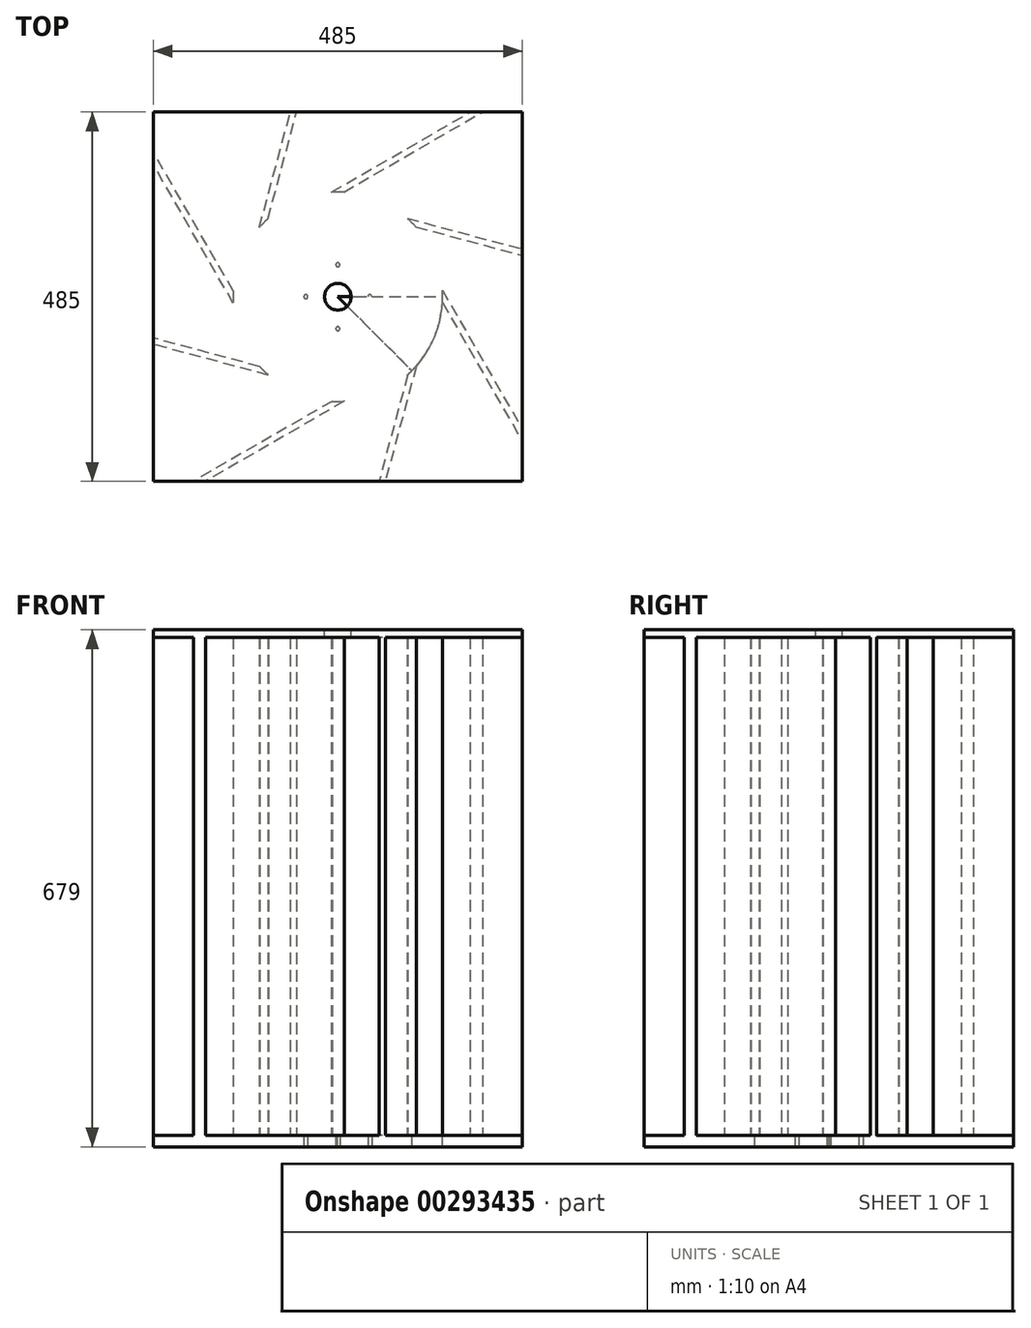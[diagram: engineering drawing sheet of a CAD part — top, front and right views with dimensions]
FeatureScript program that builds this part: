
annotation { "Feature Type Name" : "Feature", "Feature Type Description" : "" }
export const myFeature = defineFeature(function(context is Context, id is Id, definition is map)
    precondition{}
    {
        {
            var Q0;
            Q0=qCreatedBy(makeId("Top.planeOp"),FACE);
            var sketch = newSketch(context, id + "F0", { "sketchPlane" : qUnion([Q0])});
            skCircle(sketch, "E0", {"center": v(0, 0) * mm, "radius": 135 * mm});
            skLineSegment(sketch, "E1.bottom", {"start": v(242.5, -242.5) * mm, "end": v(-242.5, -242.5) * mm});
            skLineSegment(sketch, "E1.top", {"start": v(242.5, 242.5) * mm, "end": v(-242.5, 242.5) * mm});
            skLineSegment(sketch, "E1.left", {"start": v(242.5, -242.5) * mm, "end": v(242.5, 242.5) * mm});
            skLineSegment(sketch, "E1.right", {"start": v(-242.5, -242.5) * mm, "end": v(-242.5, 242.5) * mm});
            skCircle(sketch, "E2", {"center": v(0, 0) * mm, "radius": 137.5 * mm});
            skLineSegment(sketch, "E3", {"start": v(0, 242.5) * mm, "end": v(0, -242.5) * mm});
            skLineSegment(sketch, "E4", {"start": v(-242.5, 0) * mm, "end": v(242.5, 0) * mm});
            skLineSegment(sketch, "E5", {"start": v(-242.5, -242.5) * mm, "end": v(242.5, 242.5) * mm});
            skLineSegment(sketch, "E6", {"start": v(-242.5, 242.5) * mm, "end": v(242.5, -242.5) * mm});
            skLineSegment(sketch, "E7", {"start": v(0, 137.5) * mm, "end": v(181.87, 242.5) * mm});
            skLineSegment(sketch, "E8", {"start": v(-97.23, 97.23) * mm, "end": v(-58.3, 242.5) * mm});
            skLineSegment(sketch, "E9", {"start": v(-137.5, 0) * mm, "end": v(-242.5, 181.87) * mm});
            skLineSegment(sketch, "E10", {"start": v(-97.23, -97.23) * mm, "end": v(-242.5, -58.3) * mm});
            skLineSegment(sketch, "E11", {"start": v(0, -137.5) * mm, "end": v(-181.87, -242.5) * mm});
            skLineSegment(sketch, "E12", {"start": v(97.23, -97.23) * mm, "end": v(58.3, -242.5) * mm});
            skLineSegment(sketch, "E13", {"start": v(137.5, 0) * mm, "end": v(242.5, -181.87) * mm});
            skLineSegment(sketch, "E14", {"start": v(97.23, 97.23) * mm, "end": v(242.5, 58.3) * mm});
            skLineSegment(sketch, "E15.0", {"start": v(-91.68, 102.47) * mm, "end": v(-54.16, 242.5) * mm});
            skLineSegment(sketch, "E16.0", {"start": v(-103.02, 91.07) * mm, "end": v(-62.44, 242.5) * mm});
            skLineSegment(sketch, "E17.0", {"start": v(7.63, 137.29) * mm, "end": v(189.87, 242.5) * mm});
            skLineSegment(sketch, "E18.0", {"start": v(-8.45, 137.24) * mm, "end": v(173.87, 242.5) * mm});
            skLineSegment(sketch, "E19.0", {"start": v(102.47, 91.68) * mm, "end": v(242.5, 54.16) * mm});
            skLineSegment(sketch, "E20.0", {"start": v(91.07, 103.02) * mm, "end": v(242.5, 62.44) * mm});
            skLineSegment(sketch, "E21.0", {"start": v(137.29, -7.63) * mm, "end": v(242.5, -189.87) * mm});
            skLineSegment(sketch, "E22.0", {"start": v(137.24, 8.45) * mm, "end": v(242.5, -173.87) * mm});
            skLineSegment(sketch, "E23.0", {"start": v(-137.29, 7.63) * mm, "end": v(-242.5, 189.87) * mm});
            skLineSegment(sketch, "E24.0", {"start": v(-137.24, -8.45) * mm, "end": v(-242.5, 173.87) * mm});
            skLineSegment(sketch, "E25.0", {"start": v(-102.47, -91.68) * mm, "end": v(-242.5, -54.16) * mm});
            skLineSegment(sketch, "E26.0", {"start": v(-91.07, -103.02) * mm, "end": v(-242.5, -62.44) * mm});
            skLineSegment(sketch, "E27.0", {"start": v(-7.63, -137.29) * mm, "end": v(-189.87, -242.5) * mm});
            skLineSegment(sketch, "E28.0", {"start": v(8.45, -137.24) * mm, "end": v(-173.87, -242.5) * mm});
            skLineSegment(sketch, "E29.0", {"start": v(91.68, -102.47) * mm, "end": v(54.16, -242.5) * mm});
            skLineSegment(sketch, "E30.0", {"start": v(103.02, -91.07) * mm, "end": v(62.44, -242.5) * mm});
            skSolve(sketch);
        }
        {
            var Q0;
            {var subQ1=sQuery(id+"F0.wireOp",EDGE,"E1.top");var subQ3=sQuery(id+"F0.wireOp",EDGE,"E16.0");var subQ4=makeQuery(id+"F0.imprint","INTERSECT",VERTEX,{"derivedFrom":[subQ1,subQ3]});Q0=makeQuery(id+"F0.imprint","IMPRINT",FACE,{"disambiguationData":[TD([[makeQuery(id+"F0.imprint","IMPRINT",EDGE,{"disambiguationData":[TD([[subQ4,1.0]])],"derivedFrom":subQ3}),1.0]])]});}
            var Q1;
            {var subQ7=sQuery(id+"F0.wireOp",EDGE,"E23.0");Q1=makeQuery(id+"F0.imprint","IMPRINT",FACE,{"disambiguationData":[TD([[makeQuery(id+"F0.imprint","IMPRINT",EDGE,{"derivedFrom":subQ7}),-1.0]])]});}
            var Q2;
            {var subQ0=sQuery(id+"F0.wireOp",EDGE,"E5");var subQ5=sQuery(id+"F0.wireOp",EDGE,"E0");var subQ6=makeQuery(id+"F0.imprint","INTERSECT",VERTEX,{"disambiguationData":[OD(0.0)],"derivedFrom":[subQ5,subQ0]});Q2=makeQuery(id+"F0.imprint","IMPRINT",FACE,{"disambiguationData":[TD([[makeQuery(id+"F0.imprint","IMPRINT",EDGE,{"disambiguationData":[TD([[subQ6,1.0]])],"derivedFrom":subQ5}),-1.0]])]});}
            var Q3;
            {var subQ0=sQuery(id+"F0.wireOp",EDGE,"E5");var subQ1=sQuery(id+"F0.wireOp",EDGE,"E0");var subQ2=makeQuery(id+"F0.imprint","INTERSECT",VERTEX,{"disambiguationData":[OD(1.0)],"derivedFrom":[subQ1,subQ0]});Q3=makeQuery(id+"F0.imprint","IMPRINT",FACE,{"disambiguationData":[TD([[makeQuery(id+"F0.imprint","IMPRINT",EDGE,{"disambiguationData":[TD([[subQ2,-1.0]])],"derivedFrom":subQ1}),1.0]])]});}
            var Q4;
            {var subQ5=sQuery(id+"F0.wireOp",EDGE,"E29.0");Q4=makeQuery(id+"F0.imprint","IMPRINT",FACE,{"disambiguationData":[TD([[makeQuery(id+"F0.imprint","IMPRINT",EDGE,{"derivedFrom":subQ5}),-1.0]])]});}
            var Q5;
            {var subQ1=sQuery(id+"F0.wireOp",EDGE,"E1.bottom");var subQ3=sQuery(id+"F0.wireOp",EDGE,"E30.0");var subQ4=makeQuery(id+"F0.imprint","INTERSECT",VERTEX,{"derivedFrom":[subQ1,subQ3]});Q5=makeQuery(id+"F0.imprint","IMPRINT",FACE,{"disambiguationData":[TD([[makeQuery(id+"F0.imprint","IMPRINT",EDGE,{"disambiguationData":[TD([[subQ4,1.0]])],"derivedFrom":subQ3}),1.0]])]});}
            var Q6;
            {var subQ0=sQuery(id+"F0.wireOp",EDGE,"E3");var subQ1=sQuery(id+"F0.wireOp",EDGE,"E1.bottom");var subQ2=makeQuery(id+"F0.imprint","INTERSECT",VERTEX,{"derivedFrom":[subQ1,subQ0]});Q6=makeQuery(id+"F0.imprint","IMPRINT",FACE,{"disambiguationData":[TD([[makeQuery(id+"F0.imprint","IMPRINT",EDGE,{"disambiguationData":[TD([[subQ2,-1.0]])],"derivedFrom":subQ1}),-1.0]])]});}
            var Q7;
            {var subQ0=sQuery(id+"F0.wireOp",EDGE,"E3");var subQ1=sQuery(id+"F0.wireOp",EDGE,"E0");var subQ2=makeQuery(id+"F0.imprint","INTERSECT",VERTEX,{"disambiguationData":[OD(1.0)],"derivedFrom":[subQ1,subQ0]});Q7=makeQuery(id+"F0.imprint","IMPRINT",FACE,{"disambiguationData":[TD([[makeQuery(id+"F0.imprint","IMPRINT",EDGE,{"disambiguationData":[TD([[subQ2,-1.0]])],"derivedFrom":subQ1}),1.0]])]});}
            var Q8;
            {var subQ0=sQuery(id+"F0.wireOp",EDGE,"E4");var subQ1=sQuery(id+"F0.wireOp",EDGE,"E0");var subQ2=makeQuery(id+"F0.imprint","INTERSECT",VERTEX,{"disambiguationData":[OD(0.0)],"derivedFrom":[subQ1,subQ0]});Q8=makeQuery(id+"F0.imprint","IMPRINT",FACE,{"disambiguationData":[TD([[makeQuery(id+"F0.imprint","IMPRINT",EDGE,{"disambiguationData":[TD([[subQ2,1.0]])],"derivedFrom":subQ1}),1.0]])]});}
            var Q9;
            {var subQ4=sQuery(id+"F0.wireOp",EDGE,"E0");var subQ7=sQuery(id+"F0.wireOp",EDGE,"E3");var subQ9=makeQuery(id+"F0.imprint","INTERSECT",VERTEX,{"disambiguationData":[OD(1.0)],"derivedFrom":[subQ4,subQ7]});Q9=makeQuery(id+"F0.imprint","IMPRINT",FACE,{"disambiguationData":[TD([[makeQuery(id+"F0.imprint","IMPRINT",EDGE,{"disambiguationData":[TD([[subQ9,-1.0]])],"derivedFrom":subQ4}),-1.0]])]});}
            var Q10;
            {var subQ4=sQuery(id+"F0.wireOp",EDGE,"E3");var subQ7=sQuery(id+"F0.wireOp",EDGE,"E0");var subQ8=makeQuery(id+"F0.imprint","INTERSECT",VERTEX,{"disambiguationData":[OD(0.0)],"derivedFrom":[subQ7,subQ4]});Q10=makeQuery(id+"F0.imprint","IMPRINT",FACE,{"disambiguationData":[TD([[makeQuery(id+"F0.imprint","IMPRINT",EDGE,{"disambiguationData":[TD([[subQ8,-1.0]])],"derivedFrom":subQ7}),-1.0]])]});}
            var Q11;
            {var subQ0=sQuery(id+"F0.wireOp",EDGE,"E21.0");Q11=makeQuery(id+"F0.imprint","IMPRINT",FACE,{"disambiguationData":[TD([[makeQuery(id+"F0.imprint","IMPRINT",EDGE,{"derivedFrom":subQ0}),-1.0]])]});}
            var Q12;
            {var subQ0=sQuery(id+"F0.wireOp",EDGE,"E4");var subQ7=sQuery(id+"F0.wireOp",EDGE,"E0");var subQ8=makeQuery(id+"F0.imprint","INTERSECT",VERTEX,{"disambiguationData":[OD(0.0)],"derivedFrom":[subQ7,subQ0]});Q12=makeQuery(id+"F0.imprint","IMPRINT",FACE,{"disambiguationData":[TD([[makeQuery(id+"F0.imprint","IMPRINT",EDGE,{"disambiguationData":[TD([[subQ8,1.0]])],"derivedFrom":subQ7}),-1.0]])]});}
            var Q13;
            {var subQ0=sQuery(id+"F0.wireOp",EDGE,"E4");var subQ1=sQuery(id+"F0.wireOp",EDGE,"E0");var subQ2=makeQuery(id+"F0.imprint","INTERSECT",VERTEX,{"disambiguationData":[OD(1.0)],"derivedFrom":[subQ1,subQ0]});Q13=makeQuery(id+"F0.imprint","IMPRINT",FACE,{"disambiguationData":[TD([[makeQuery(id+"F0.imprint","IMPRINT",EDGE,{"disambiguationData":[TD([[subQ2,-1.0]])],"derivedFrom":subQ1}),1.0]])]});}
            var Q14;
            {var subQ0=sQuery(id+"F0.wireOp",EDGE,"E6");var subQ1=sQuery(id+"F0.wireOp",EDGE,"E0");var subQ2=makeQuery(id+"F0.imprint","INTERSECT",VERTEX,{"disambiguationData":[OD(0.0)],"derivedFrom":[subQ1,subQ0]});Q14=makeQuery(id+"F0.imprint","IMPRINT",FACE,{"disambiguationData":[TD([[makeQuery(id+"F0.imprint","IMPRINT",EDGE,{"disambiguationData":[TD([[subQ2,-1.0]])],"derivedFrom":subQ1}),1.0]])]});}
            var Q15;
            {var subQ4=sQuery(id+"F0.wireOp",EDGE,"E5");var subQ5=sQuery(id+"F0.wireOp",EDGE,"E0");var subQ6=makeQuery(id+"F0.imprint","INTERSECT",VERTEX,{"disambiguationData":[OD(0.0)],"derivedFrom":[subQ5,subQ4]});Q15=makeQuery(id+"F0.imprint","IMPRINT",FACE,{"disambiguationData":[TD([[makeQuery(id+"F0.imprint","IMPRINT",EDGE,{"disambiguationData":[TD([[subQ6,-1.0]])],"derivedFrom":subQ5}),-1.0]])]});}
            var Q16;
            {var subQ7=sQuery(id+"F0.wireOp",EDGE,"E25.0");Q16=makeQuery(id+"F0.imprint","IMPRINT",FACE,{"disambiguationData":[TD([[makeQuery(id+"F0.imprint","IMPRINT",EDGE,{"derivedFrom":subQ7}),-1.0]])]});}
            var Q17;
            {var subQ5=sQuery(id+"F0.wireOp",EDGE,"E5");var subQ7=sQuery(id+"F0.wireOp",EDGE,"E0");var subQ8=makeQuery(id+"F0.imprint","INTERSECT",VERTEX,{"disambiguationData":[OD(1.0)],"derivedFrom":[subQ7,subQ5]});Q17=makeQuery(id+"F0.imprint","IMPRINT",FACE,{"disambiguationData":[TD([[makeQuery(id+"F0.imprint","IMPRINT",EDGE,{"disambiguationData":[TD([[subQ8,-1.0]])],"derivedFrom":subQ7}),-1.0]])]});}
            var Q18;
            {var subQ0=sQuery(id+"F0.wireOp",EDGE,"E3");var subQ1=sQuery(id+"F0.wireOp",EDGE,"E0");var subQ2=makeQuery(id+"F0.imprint","INTERSECT",VERTEX,{"disambiguationData":[OD(0.0)],"derivedFrom":[subQ1,subQ0]});Q18=makeQuery(id+"F0.imprint","IMPRINT",FACE,{"disambiguationData":[TD([[makeQuery(id+"F0.imprint","IMPRINT",EDGE,{"disambiguationData":[TD([[subQ2,-1.0]])],"derivedFrom":subQ1}),1.0]])]});}
            var Q19;
            {var subQ0=sQuery(id+"F0.wireOp",EDGE,"E5");var subQ1=sQuery(id+"F0.wireOp",EDGE,"E0");var subQ2=makeQuery(id+"F0.imprint","INTERSECT",VERTEX,{"disambiguationData":[OD(0.0)],"derivedFrom":[subQ1,subQ0]});Q19=makeQuery(id+"F0.imprint","IMPRINT",FACE,{"disambiguationData":[TD([[makeQuery(id+"F0.imprint","IMPRINT",EDGE,{"disambiguationData":[TD([[subQ2,1.0]])],"derivedFrom":subQ1}),1.0]])]});}
            var Q20;
            {var subQ0=sQuery(id+"F0.wireOp",EDGE,"E5");var subQ1=sQuery(id+"F0.wireOp",EDGE,"E0");var subQ2=makeQuery(id+"F0.imprint","INTERSECT",VERTEX,{"disambiguationData":[OD(0.0)],"derivedFrom":[subQ1,subQ0]});Q20=makeQuery(id+"F0.imprint","IMPRINT",FACE,{"disambiguationData":[TD([[makeQuery(id+"F0.imprint","IMPRINT",EDGE,{"disambiguationData":[TD([[subQ2,-1.0]])],"derivedFrom":subQ1}),1.0]])]});}
            var Q21;
            {var subQ0=sQuery(id+"F0.wireOp",EDGE,"E4");var subQ1=sQuery(id+"F0.wireOp",EDGE,"E1.right");var subQ2=makeQuery(id+"F0.imprint","INTERSECT",VERTEX,{"derivedFrom":[subQ1,subQ0]});Q21=makeQuery(id+"F0.imprint","IMPRINT",FACE,{"disambiguationData":[TD([[makeQuery(id+"F0.imprint","IMPRINT",EDGE,{"disambiguationData":[TD([[subQ2,-1.0]])],"derivedFrom":subQ1}),-1.0]])]});}
            var Q22;
            {var subQ1=sQuery(id+"F0.wireOp",EDGE,"E1.right");var subQ3=sQuery(id+"F0.wireOp",EDGE,"E26.0");var subQ4=makeQuery(id+"F0.imprint","INTERSECT",VERTEX,{"derivedFrom":[subQ1,subQ3]});Q22=makeQuery(id+"F0.imprint","IMPRINT",FACE,{"disambiguationData":[TD([[makeQuery(id+"F0.imprint","IMPRINT",EDGE,{"disambiguationData":[TD([[subQ4,1.0]])],"derivedFrom":subQ3}),1.0]])]});}
            var Q23;
            {var subQ0=sQuery(id+"F0.wireOp",EDGE,"E4");var subQ1=sQuery(id+"F0.wireOp",EDGE,"E1.left");var subQ2=makeQuery(id+"F0.imprint","INTERSECT",VERTEX,{"derivedFrom":[subQ1,subQ0]});Q23=makeQuery(id+"F0.imprint","IMPRINT",FACE,{"disambiguationData":[TD([[makeQuery(id+"F0.imprint","IMPRINT",EDGE,{"disambiguationData":[TD([[subQ2,1.0]])],"derivedFrom":subQ1}),1.0]])]});}
            var Q24;
            {var subQ3=sQuery(id+"F0.wireOp",EDGE,"E4");var subQ5=sQuery(id+"F0.wireOp",EDGE,"E0");var subQ6=makeQuery(id+"F0.imprint","INTERSECT",VERTEX,{"disambiguationData":[OD(1.0)],"derivedFrom":[subQ5,subQ3]});Q24=makeQuery(id+"F0.imprint","IMPRINT",FACE,{"disambiguationData":[TD([[makeQuery(id+"F0.imprint","IMPRINT",EDGE,{"disambiguationData":[TD([[subQ6,-1.0]])],"derivedFrom":subQ5}),-1.0]])]});}
            var Q25;
            {var subQ0=sQuery(id+"F0.wireOp",EDGE,"E19.0");Q25=makeQuery(id+"F0.imprint","IMPRINT",FACE,{"disambiguationData":[TD([[makeQuery(id+"F0.imprint","IMPRINT",EDGE,{"derivedFrom":subQ0}),-1.0]])]});}
            var Q26;
            {var subQ3=sQuery(id+"F0.wireOp",EDGE,"E27.0");Q26=makeQuery(id+"F0.imprint","IMPRINT",FACE,{"disambiguationData":[TD([[makeQuery(id+"F0.imprint","IMPRINT",EDGE,{"derivedFrom":subQ3}),-1.0]])]});}
            var Q27;
            {var subQ5=sQuery(id+"F0.wireOp",EDGE,"E6");var subQ7=sQuery(id+"F0.wireOp",EDGE,"E0");var subQ8=makeQuery(id+"F0.imprint","INTERSECT",VERTEX,{"disambiguationData":[OD(0.0)],"derivedFrom":[subQ7,subQ5]});Q27=makeQuery(id+"F0.imprint","IMPRINT",FACE,{"disambiguationData":[TD([[makeQuery(id+"F0.imprint","IMPRINT",EDGE,{"disambiguationData":[TD([[subQ8,-1.0]])],"derivedFrom":subQ7}),-1.0]])]});}
            var Q28;
            {var subQ1=sQuery(id+"F0.wireOp",EDGE,"E2");var subQ3=sQuery(id+"F0.wireOp",EDGE,"E26.0");var subQ4=makeQuery(id+"F0.imprint","INTERSECT",VERTEX,{"derivedFrom":[subQ1,subQ3]});Q28=makeQuery(id+"F0.imprint","IMPRINT",FACE,{"disambiguationData":[TD([[makeQuery(id+"F0.imprint","IMPRINT",EDGE,{"disambiguationData":[TD([[subQ4,-1.0]])],"derivedFrom":subQ3}),-1.0]])]});}
            var Q29;
            {var subQ1=sQuery(id+"F0.wireOp",EDGE,"E2");var subQ3=sQuery(id+"F0.wireOp",EDGE,"E22.0");var subQ4=makeQuery(id+"F0.imprint","INTERSECT",VERTEX,{"derivedFrom":[subQ1,subQ3]});Q29=makeQuery(id+"F0.imprint","IMPRINT",FACE,{"disambiguationData":[TD([[makeQuery(id+"F0.imprint","IMPRINT",EDGE,{"disambiguationData":[TD([[subQ4,-1.0]])],"derivedFrom":subQ3}),-1.0]])]});}
            var Q30;
            {var subQ0=sQuery(id+"F0.wireOp",EDGE,"E11");Q30=makeQuery(id+"F0.imprint","IMPRINT",FACE,{"disambiguationData":[TD([[makeQuery(id+"F0.imprint","IMPRINT",EDGE,{"derivedFrom":subQ0}),1.0]])]});}
            var Q31;
            {var subQ0=sQuery(id+"F0.wireOp",EDGE,"E13");Q31=makeQuery(id+"F0.imprint","IMPRINT",FACE,{"disambiguationData":[TD([[makeQuery(id+"F0.imprint","IMPRINT",EDGE,{"derivedFrom":subQ0}),-1.0]])]});}
            var Q32;
            {var subQ0=sQuery(id+"F0.wireOp",EDGE,"E12");Q32=makeQuery(id+"F0.imprint","IMPRINT",FACE,{"disambiguationData":[TD([[makeQuery(id+"F0.imprint","IMPRINT",EDGE,{"derivedFrom":subQ0}),1.0]])]});}
            var Q33;
            {var subQ0=sQuery(id+"F0.wireOp",EDGE,"E8");Q33=makeQuery(id+"F0.imprint","IMPRINT",FACE,{"disambiguationData":[TD([[makeQuery(id+"F0.imprint","IMPRINT",EDGE,{"derivedFrom":subQ0}),-1.0]])]});}
            var Q34;
            {var subQ1=sQuery(id+"F0.wireOp",EDGE,"E2");var subQ3=sQuery(id+"F0.wireOp",EDGE,"E28.0");var subQ4=makeQuery(id+"F0.imprint","INTERSECT",VERTEX,{"derivedFrom":[subQ1,subQ3]});Q34=makeQuery(id+"F0.imprint","IMPRINT",FACE,{"disambiguationData":[TD([[makeQuery(id+"F0.imprint","IMPRINT",EDGE,{"disambiguationData":[TD([[subQ4,-1.0]])],"derivedFrom":subQ3}),-1.0]])]});}
            var Q35;
            {var subQ1=sQuery(id+"F0.wireOp",EDGE,"E2");var subQ3=sQuery(id+"F0.wireOp",EDGE,"E18.0");var subQ4=makeQuery(id+"F0.imprint","INTERSECT",VERTEX,{"derivedFrom":[subQ1,subQ3]});Q35=makeQuery(id+"F0.imprint","IMPRINT",FACE,{"disambiguationData":[TD([[makeQuery(id+"F0.imprint","IMPRINT",EDGE,{"disambiguationData":[TD([[subQ4,-1.0]])],"derivedFrom":subQ3}),-1.0]])]});}
            var Q36;
            {var subQ0=sQuery(id+"F0.wireOp",EDGE,"E10");Q36=makeQuery(id+"F0.imprint","IMPRINT",FACE,{"disambiguationData":[TD([[makeQuery(id+"F0.imprint","IMPRINT",EDGE,{"derivedFrom":subQ0}),1.0]])]});}
            var Q37;
            {var subQ0=sQuery(id+"F0.wireOp",EDGE,"E12");Q37=makeQuery(id+"F0.imprint","IMPRINT",FACE,{"disambiguationData":[TD([[makeQuery(id+"F0.imprint","IMPRINT",EDGE,{"derivedFrom":subQ0}),-1.0]])]});}
            var Q38;
            {var subQ0=sQuery(id+"F0.wireOp",EDGE,"E9");Q38=makeQuery(id+"F0.imprint","IMPRINT",FACE,{"disambiguationData":[TD([[makeQuery(id+"F0.imprint","IMPRINT",EDGE,{"derivedFrom":subQ0}),1.0]])]});}
            var Q39;
            {var subQ0=sQuery(id+"F0.wireOp",EDGE,"E8");Q39=makeQuery(id+"F0.imprint","IMPRINT",FACE,{"disambiguationData":[TD([[makeQuery(id+"F0.imprint","IMPRINT",EDGE,{"derivedFrom":subQ0}),1.0]])]});}
            var Q40;
            {var subQ0=sQuery(id+"F0.wireOp",EDGE,"E14");Q40=makeQuery(id+"F0.imprint","IMPRINT",FACE,{"disambiguationData":[TD([[makeQuery(id+"F0.imprint","IMPRINT",EDGE,{"derivedFrom":subQ0}),1.0]])]});}
            var Q41;
            {var subQ0=sQuery(id+"F0.wireOp",EDGE,"E10");Q41=makeQuery(id+"F0.imprint","IMPRINT",FACE,{"disambiguationData":[TD([[makeQuery(id+"F0.imprint","IMPRINT",EDGE,{"derivedFrom":subQ0}),-1.0]])]});}
            var Q42;
            {var subQ0=sQuery(id+"F0.wireOp",EDGE,"E14");Q42=makeQuery(id+"F0.imprint","IMPRINT",FACE,{"disambiguationData":[TD([[makeQuery(id+"F0.imprint","IMPRINT",EDGE,{"derivedFrom":subQ0}),-1.0]])]});}
            var Q43;
            {var subQ0=sQuery(id+"F0.wireOp",EDGE,"E9");Q43=makeQuery(id+"F0.imprint","IMPRINT",FACE,{"disambiguationData":[TD([[makeQuery(id+"F0.imprint","IMPRINT",EDGE,{"derivedFrom":subQ0}),-1.0]])]});}
            var Q44;
            {var subQ1=sQuery(id+"F0.wireOp",EDGE,"E2");var subQ3=sQuery(id+"F0.wireOp",EDGE,"E16.0");var subQ4=makeQuery(id+"F0.imprint","INTERSECT",VERTEX,{"derivedFrom":[subQ1,subQ3]});Q44=makeQuery(id+"F0.imprint","IMPRINT",FACE,{"disambiguationData":[TD([[makeQuery(id+"F0.imprint","IMPRINT",EDGE,{"disambiguationData":[TD([[subQ4,-1.0]])],"derivedFrom":subQ3}),-1.0]])]});}
            var Q45;
            {var subQ0=sQuery(id+"F0.wireOp",EDGE,"E13");Q45=makeQuery(id+"F0.imprint","IMPRINT",FACE,{"disambiguationData":[TD([[makeQuery(id+"F0.imprint","IMPRINT",EDGE,{"derivedFrom":subQ0}),1.0]])]});}
            var Q46;
            {var subQ0=sQuery(id+"F0.wireOp",EDGE,"E11");Q46=makeQuery(id+"F0.imprint","IMPRINT",FACE,{"disambiguationData":[TD([[makeQuery(id+"F0.imprint","IMPRINT",EDGE,{"derivedFrom":subQ0}),-1.0]])]});}
            var Q47;
            {var subQ1=sQuery(id+"F0.wireOp",EDGE,"E2");var subQ3=sQuery(id+"F0.wireOp",EDGE,"E20.0");var subQ4=makeQuery(id+"F0.imprint","INTERSECT",VERTEX,{"derivedFrom":[subQ1,subQ3]});Q47=makeQuery(id+"F0.imprint","IMPRINT",FACE,{"disambiguationData":[TD([[makeQuery(id+"F0.imprint","IMPRINT",EDGE,{"disambiguationData":[TD([[subQ4,-1.0]])],"derivedFrom":subQ3}),-1.0]])]});}
            var Q48;
            {var subQ1=sQuery(id+"F0.wireOp",EDGE,"E2");var subQ3=sQuery(id+"F0.wireOp",EDGE,"E30.0");var subQ4=makeQuery(id+"F0.imprint","INTERSECT",VERTEX,{"derivedFrom":[subQ1,subQ3]});Q48=makeQuery(id+"F0.imprint","IMPRINT",FACE,{"disambiguationData":[TD([[makeQuery(id+"F0.imprint","IMPRINT",EDGE,{"disambiguationData":[TD([[subQ4,-1.0]])],"derivedFrom":subQ3}),-1.0]])]});}
            var Q49;
            {var subQ1=sQuery(id+"F0.wireOp",EDGE,"E2");var subQ3=sQuery(id+"F0.wireOp",EDGE,"E24.0");var subQ4=makeQuery(id+"F0.imprint","INTERSECT",VERTEX,{"derivedFrom":[subQ1,subQ3]});Q49=makeQuery(id+"F0.imprint","IMPRINT",FACE,{"disambiguationData":[TD([[makeQuery(id+"F0.imprint","IMPRINT",EDGE,{"disambiguationData":[TD([[subQ4,-1.0]])],"derivedFrom":subQ3}),-1.0]])]});}
            var Q50;
            {var subQ0=sQuery(id+"F0.wireOp",EDGE,"E15.0");Q50=makeQuery(id+"F0.imprint","IMPRINT",FACE,{"disambiguationData":[TD([[makeQuery(id+"F0.imprint","IMPRINT",EDGE,{"derivedFrom":subQ0}),-1.0]])]});}
            var Q51;
            {var subQ1=sQuery(id+"F0.wireOp",EDGE,"E1.left");var subQ3=sQuery(id+"F0.wireOp",EDGE,"E20.0");var subQ4=makeQuery(id+"F0.imprint","INTERSECT",VERTEX,{"derivedFrom":[subQ1,subQ3]});Q51=makeQuery(id+"F0.imprint","IMPRINT",FACE,{"disambiguationData":[TD([[makeQuery(id+"F0.imprint","IMPRINT",EDGE,{"disambiguationData":[TD([[subQ4,1.0]])],"derivedFrom":subQ3}),1.0]])]});}
            var Q52;
            {var subQ0=sQuery(id+"F0.wireOp",EDGE,"E3");var subQ1=sQuery(id+"F0.wireOp",EDGE,"E1.top");var subQ2=makeQuery(id+"F0.imprint","INTERSECT",VERTEX,{"derivedFrom":[subQ1,subQ0]});Q52=makeQuery(id+"F0.imprint","IMPRINT",FACE,{"disambiguationData":[TD([[makeQuery(id+"F0.imprint","IMPRINT",EDGE,{"disambiguationData":[TD([[subQ2,1.0]])],"derivedFrom":subQ1}),1.0]])]});}
            var Q53;
            {var subQ0=sQuery(id+"F0.wireOp",EDGE,"E17.0");Q53=makeQuery(id+"F0.imprint","IMPRINT",FACE,{"disambiguationData":[TD([[makeQuery(id+"F0.imprint","IMPRINT",EDGE,{"derivedFrom":subQ0}),-1.0]])]});}
            var Q54;
            {var subQ0=sQuery(id+"F0.wireOp",EDGE,"E7");Q54=makeQuery(id+"F0.imprint","IMPRINT",FACE,{"disambiguationData":[TD([[makeQuery(id+"F0.imprint","IMPRINT",EDGE,{"derivedFrom":subQ0}),1.0]])]});}
            var Q55;
            {var subQ0=sQuery(id+"F0.wireOp",EDGE,"E7");Q55=makeQuery(id+"F0.imprint","IMPRINT",FACE,{"disambiguationData":[TD([[makeQuery(id+"F0.imprint","IMPRINT",EDGE,{"derivedFrom":subQ0}),-1.0]])]});}
            extrude(context, id + "F1", {"entities" : qUnion([Q0, Q1, Q2, Q3, Q4, Q5, Q6, Q7, Q8, Q9, Q10, Q11, Q12, Q13, Q14, Q15, Q16, Q17, Q18, Q19, Q20, Q21, Q22, Q23, Q24, Q25, Q26, Q27, Q28, Q29, Q30, Q31, Q32, Q33, Q34, Q35, Q36, Q37, Q38, Q39, Q40, Q41, Q42, Q43, Q44, Q45, Q46, Q47, Q48, Q49, Q50, Q51, Q52, Q53, Q54, Q55]), "oppositeDirection" : true, "depth" : 15 * mm});
        }
        {
            var Q0;
            {var subQ0=sQuery(id+"F0.wireOp",EDGE,"E8");Q0=makeQuery(id+"F0.imprint","IMPRINT",FACE,{"disambiguationData":[TD([[makeQuery(id+"F0.imprint","IMPRINT",EDGE,{"derivedFrom":subQ0}),1.0]])]});}
            var Q1;
            {var subQ0=sQuery(id+"F0.wireOp",EDGE,"E8");Q1=makeQuery(id+"F0.imprint","IMPRINT",FACE,{"disambiguationData":[TD([[makeQuery(id+"F0.imprint","IMPRINT",EDGE,{"derivedFrom":subQ0}),-1.0]])]});}
            var Q2;
            {var subQ1=sQuery(id+"F0.wireOp",EDGE,"E2");var subQ3=sQuery(id+"F0.wireOp",EDGE,"E16.0");var subQ4=makeQuery(id+"F0.imprint","INTERSECT",VERTEX,{"derivedFrom":[subQ1,subQ3]});Q2=makeQuery(id+"F0.imprint","IMPRINT",FACE,{"disambiguationData":[TD([[makeQuery(id+"F0.imprint","IMPRINT",EDGE,{"disambiguationData":[TD([[subQ4,-1.0]])],"derivedFrom":subQ3}),-1.0]])]});}
            var Q3;
            {var subQ0=sQuery(id+"F0.wireOp",EDGE,"E7");Q3=makeQuery(id+"F0.imprint","IMPRINT",FACE,{"disambiguationData":[TD([[makeQuery(id+"F0.imprint","IMPRINT",EDGE,{"derivedFrom":subQ0}),1.0]])]});}
            var Q4;
            {var subQ0=sQuery(id+"F0.wireOp",EDGE,"E7");Q4=makeQuery(id+"F0.imprint","IMPRINT",FACE,{"disambiguationData":[TD([[makeQuery(id+"F0.imprint","IMPRINT",EDGE,{"derivedFrom":subQ0}),-1.0]])]});}
            var Q5;
            {var subQ1=sQuery(id+"F0.wireOp",EDGE,"E2");var subQ3=sQuery(id+"F0.wireOp",EDGE,"E18.0");var subQ4=makeQuery(id+"F0.imprint","INTERSECT",VERTEX,{"derivedFrom":[subQ1,subQ3]});Q5=makeQuery(id+"F0.imprint","IMPRINT",FACE,{"disambiguationData":[TD([[makeQuery(id+"F0.imprint","IMPRINT",EDGE,{"disambiguationData":[TD([[subQ4,-1.0]])],"derivedFrom":subQ3}),-1.0]])]});}
            var Q6;
            {var subQ0=sQuery(id+"F0.wireOp",EDGE,"E14");Q6=makeQuery(id+"F0.imprint","IMPRINT",FACE,{"disambiguationData":[TD([[makeQuery(id+"F0.imprint","IMPRINT",EDGE,{"derivedFrom":subQ0}),-1.0]])]});}
            var Q7;
            {var subQ0=sQuery(id+"F0.wireOp",EDGE,"E14");Q7=makeQuery(id+"F0.imprint","IMPRINT",FACE,{"disambiguationData":[TD([[makeQuery(id+"F0.imprint","IMPRINT",EDGE,{"derivedFrom":subQ0}),1.0]])]});}
            var Q8;
            {var subQ1=sQuery(id+"F0.wireOp",EDGE,"E2");var subQ3=sQuery(id+"F0.wireOp",EDGE,"E20.0");var subQ4=makeQuery(id+"F0.imprint","INTERSECT",VERTEX,{"derivedFrom":[subQ1,subQ3]});Q8=makeQuery(id+"F0.imprint","IMPRINT",FACE,{"disambiguationData":[TD([[makeQuery(id+"F0.imprint","IMPRINT",EDGE,{"disambiguationData":[TD([[subQ4,-1.0]])],"derivedFrom":subQ3}),-1.0]])]});}
            var Q9;
            {var subQ1=sQuery(id+"F0.wireOp",EDGE,"E2");var subQ3=sQuery(id+"F0.wireOp",EDGE,"E22.0");var subQ4=makeQuery(id+"F0.imprint","INTERSECT",VERTEX,{"derivedFrom":[subQ1,subQ3]});Q9=makeQuery(id+"F0.imprint","IMPRINT",FACE,{"disambiguationData":[TD([[makeQuery(id+"F0.imprint","IMPRINT",EDGE,{"disambiguationData":[TD([[subQ4,-1.0]])],"derivedFrom":subQ3}),-1.0]])]});}
            var Q10;
            {var subQ0=sQuery(id+"F0.wireOp",EDGE,"E13");Q10=makeQuery(id+"F0.imprint","IMPRINT",FACE,{"disambiguationData":[TD([[makeQuery(id+"F0.imprint","IMPRINT",EDGE,{"derivedFrom":subQ0}),1.0]])]});}
            var Q11;
            {var subQ0=sQuery(id+"F0.wireOp",EDGE,"E13");Q11=makeQuery(id+"F0.imprint","IMPRINT",FACE,{"disambiguationData":[TD([[makeQuery(id+"F0.imprint","IMPRINT",EDGE,{"derivedFrom":subQ0}),-1.0]])]});}
            var Q12;
            {var subQ0=sQuery(id+"F0.wireOp",EDGE,"E12");Q12=makeQuery(id+"F0.imprint","IMPRINT",FACE,{"disambiguationData":[TD([[makeQuery(id+"F0.imprint","IMPRINT",EDGE,{"derivedFrom":subQ0}),-1.0]])]});}
            var Q13;
            {var subQ0=sQuery(id+"F0.wireOp",EDGE,"E12");Q13=makeQuery(id+"F0.imprint","IMPRINT",FACE,{"disambiguationData":[TD([[makeQuery(id+"F0.imprint","IMPRINT",EDGE,{"derivedFrom":subQ0}),1.0]])]});}
            var Q14;
            {var subQ1=sQuery(id+"F0.wireOp",EDGE,"E2");var subQ3=sQuery(id+"F0.wireOp",EDGE,"E30.0");var subQ4=makeQuery(id+"F0.imprint","INTERSECT",VERTEX,{"derivedFrom":[subQ1,subQ3]});Q14=makeQuery(id+"F0.imprint","IMPRINT",FACE,{"disambiguationData":[TD([[makeQuery(id+"F0.imprint","IMPRINT",EDGE,{"disambiguationData":[TD([[subQ4,-1.0]])],"derivedFrom":subQ3}),-1.0]])]});}
            var Q15;
            {var subQ0=sQuery(id+"F0.wireOp",EDGE,"E11");Q15=makeQuery(id+"F0.imprint","IMPRINT",FACE,{"disambiguationData":[TD([[makeQuery(id+"F0.imprint","IMPRINT",EDGE,{"derivedFrom":subQ0}),-1.0]])]});}
            var Q16;
            {var subQ0=sQuery(id+"F0.wireOp",EDGE,"E11");Q16=makeQuery(id+"F0.imprint","IMPRINT",FACE,{"disambiguationData":[TD([[makeQuery(id+"F0.imprint","IMPRINT",EDGE,{"derivedFrom":subQ0}),1.0]])]});}
            var Q17;
            {var subQ1=sQuery(id+"F0.wireOp",EDGE,"E2");var subQ3=sQuery(id+"F0.wireOp",EDGE,"E28.0");var subQ4=makeQuery(id+"F0.imprint","INTERSECT",VERTEX,{"derivedFrom":[subQ1,subQ3]});Q17=makeQuery(id+"F0.imprint","IMPRINT",FACE,{"disambiguationData":[TD([[makeQuery(id+"F0.imprint","IMPRINT",EDGE,{"disambiguationData":[TD([[subQ4,-1.0]])],"derivedFrom":subQ3}),-1.0]])]});}
            var Q18;
            {var subQ1=sQuery(id+"F0.wireOp",EDGE,"E2");var subQ3=sQuery(id+"F0.wireOp",EDGE,"E26.0");var subQ4=makeQuery(id+"F0.imprint","INTERSECT",VERTEX,{"derivedFrom":[subQ1,subQ3]});Q18=makeQuery(id+"F0.imprint","IMPRINT",FACE,{"disambiguationData":[TD([[makeQuery(id+"F0.imprint","IMPRINT",EDGE,{"disambiguationData":[TD([[subQ4,-1.0]])],"derivedFrom":subQ3}),-1.0]])]});}
            var Q19;
            {var subQ0=sQuery(id+"F0.wireOp",EDGE,"E10");Q19=makeQuery(id+"F0.imprint","IMPRINT",FACE,{"disambiguationData":[TD([[makeQuery(id+"F0.imprint","IMPRINT",EDGE,{"derivedFrom":subQ0}),1.0]])]});}
            var Q20;
            {var subQ0=sQuery(id+"F0.wireOp",EDGE,"E10");Q20=makeQuery(id+"F0.imprint","IMPRINT",FACE,{"disambiguationData":[TD([[makeQuery(id+"F0.imprint","IMPRINT",EDGE,{"derivedFrom":subQ0}),-1.0]])]});}
            var Q21;
            {var subQ0=sQuery(id+"F0.wireOp",EDGE,"E9");Q21=makeQuery(id+"F0.imprint","IMPRINT",FACE,{"disambiguationData":[TD([[makeQuery(id+"F0.imprint","IMPRINT",EDGE,{"derivedFrom":subQ0}),-1.0]])]});}
            var Q22;
            {var subQ0=sQuery(id+"F0.wireOp",EDGE,"E9");Q22=makeQuery(id+"F0.imprint","IMPRINT",FACE,{"disambiguationData":[TD([[makeQuery(id+"F0.imprint","IMPRINT",EDGE,{"derivedFrom":subQ0}),1.0]])]});}
            var Q23;
            {var subQ1=sQuery(id+"F0.wireOp",EDGE,"E2");var subQ3=sQuery(id+"F0.wireOp",EDGE,"E24.0");var subQ4=makeQuery(id+"F0.imprint","INTERSECT",VERTEX,{"derivedFrom":[subQ1,subQ3]});Q23=makeQuery(id+"F0.imprint","IMPRINT",FACE,{"disambiguationData":[TD([[makeQuery(id+"F0.imprint","IMPRINT",EDGE,{"disambiguationData":[TD([[subQ4,-1.0]])],"derivedFrom":subQ3}),-1.0]])]});}
            extrude(context, id + "F2", {"entities" : qUnion([Q0, Q1, Q2, Q3, Q4, Q5, Q6, Q7, Q8, Q9, Q10, Q11, Q12, Q13, Q14, Q15, Q16, Q17, Q18, Q19, Q20, Q21, Q22, Q23]), "operationType" : NewBodyOperationType.ADD, "depth" : 654 * mm, "offsetDistance" : 25 * mm});
        }
        {
            var Q0;
            Q0=makeQuery(id+"F2.opExtrude","CAP_FACE",FACE,{"disambiguationData":[OSD([sQuery(id+"F0.wireOp",EDGE,"E1.left"),sQuery(id+"F0.wireOp",EDGE,"E2"),sQuery(id+"F0.wireOp",EDGE,"E19.0"),sQuery(id+"F0.wireOp",EDGE,"E20.0")])],"isStart":false});
            var sketch = newSketch(context, id + "F3", { "sketchPlane" : qUnion([Q0])});
            skLineSegment(sketch, "E31.bottom", {"start": v(242.5, -242.5) * mm, "end": v(-242.5, -242.5) * mm});
            skLineSegment(sketch, "E31.top", {"start": v(242.5, 242.5) * mm, "end": v(-242.5, 242.5) * mm});
            skLineSegment(sketch, "E31.left", {"start": v(242.5, -242.5) * mm, "end": v(242.5, 242.5) * mm});
            skLineSegment(sketch, "E31.right", {"start": v(-242.5, -242.5) * mm, "end": v(-242.5, 242.5) * mm});
            skPoint(sketch, "E31.middle", {"position": v(0, 0) * mm});
            skSolve(sketch);
        }
        {
            var Q0;
            {var subQ1=sQuery(id+"F0.wireOp",EDGE,"E19.0");var subQ2=makeQuery(id+"F2.opExtrude","CAP_EDGE",EDGE,{"disambiguationData":[OSD([subQ1])],"isStart":false});Q0=makeQuery(id+"F3.imprint","IMPRINT",FACE,{"disambiguationData":[TD([[makeQuery(id+"F3.imprint","IMPRINT",EDGE,{"derivedFrom":subQ2}),1.0]])]});}
            var Q1;
            {var subQ6=sQuery(id+"F3.wireOp",EDGE,"E31.bottom");Q1=makeQuery(id+"F3.imprint","IMPRINT",FACE,{"disambiguationData":[TD([[makeQuery(id+"F3.imprint","IMPRINT",EDGE,{"derivedFrom":subQ6}),-1.0]])]});}
            extrude(context, id + "F4", {"entities" : qUnion([Q0, Q1]), "operationType" : NewBodyOperationType.ADD, "depth" : 10 * mm});
        }
        {
            var Q0;
            Q0=makeQuery(id+"F4.opExtrude","CAP_FACE",FACE,{"disambiguationData":[OSD([sQuery(id+"F3.wireOp",EDGE,"E31.bottom"),sQuery(id+"F3.wireOp",EDGE,"E31.top"),sQuery(id+"F3.wireOp",EDGE,"E31.left"),sQuery(id+"F3.wireOp",EDGE,"E31.right")])],"isStart":false});
            var sketch = newSketch(context, id + "F5", { "sketchPlane" : qUnion([Q0])});
            skCircle(sketch, "E32", {"center": v(0, 0) * mm, "radius": 17.5 * mm});
            skLineSegment(sketch, "E33.bottom", {"start": v(28.5, -28.5) * mm, "end": v(-28.5, -28.5) * mm});
            skLineSegment(sketch, "E33.top", {"start": v(28.5, 28.5) * mm, "end": v(-28.5, 28.5) * mm});
            skLineSegment(sketch, "E33.left", {"start": v(28.5, -28.5) * mm, "end": v(28.5, 28.5) * mm});
            skLineSegment(sketch, "E33.right", {"start": v(-28.5, -28.5) * mm, "end": v(-28.5, 28.5) * mm});
            skCircle(sketch, "E34", {"center": v(0, 0) * mm, "radius": 27.5 * mm});
            skLineSegment(sketch, "E35", {"start": v(-28.5, 28.5) * mm, "end": v(28.5, -28.5) * mm});
            skLineSegment(sketch, "E36", {"start": v(28.5, 28.5) * mm, "end": v(-28.5, -28.5) * mm});
            skCircle(sketch, "E37", {"center": v(-19.45, 19.45) * mm, "radius": 4 * mm});
            skCircle(sketch, "E38", {"center": v(19.45, 19.45) * mm, "radius": 4 * mm});
            skCircle(sketch, "E39", {"center": v(-19.45, -19.45) * mm, "radius": 4 * mm});
            skCircle(sketch, "E40", {"center": v(19.45, -19.45) * mm, "radius": 4 * mm});
            skSolve(sketch);
        }
        {
            var Q0;
            {var subQ0=sQuery(id+"F5.wireOp",EDGE,"E35");var subQ1=sQuery(id+"F5.wireOp",EDGE,"E32");var subQ2=makeQuery(id+"F5.imprint","INTERSECT",VERTEX,{"disambiguationData":[OD(0.0)],"derivedFrom":[subQ1,subQ0]});Q0=makeQuery(id+"F5.imprint","IMPRINT",FACE,{"disambiguationData":[TD([[makeQuery(id+"F5.imprint","IMPRINT",EDGE,{"disambiguationData":[TD([[subQ2,-1.0]])],"derivedFrom":subQ1}),1.0]])]});}
            var Q1;
            {var subQ0=sQuery(id+"F5.wireOp",EDGE,"E35");var subQ1=sQuery(id+"F5.wireOp",EDGE,"E32");var subQ2=makeQuery(id+"F5.imprint","INTERSECT",VERTEX,{"disambiguationData":[OD(0.0)],"derivedFrom":[subQ1,subQ0]});Q1=makeQuery(id+"F5.imprint","IMPRINT",FACE,{"disambiguationData":[TD([[makeQuery(id+"F5.imprint","IMPRINT",EDGE,{"disambiguationData":[TD([[subQ2,1.0]])],"derivedFrom":subQ1}),1.0]])]});}
            var Q2;
            {var subQ0=sQuery(id+"F5.wireOp",EDGE,"E36");var subQ1=sQuery(id+"F5.wireOp",EDGE,"E32");var subQ2=makeQuery(id+"F5.imprint","INTERSECT",VERTEX,{"disambiguationData":[OD(0.0)],"derivedFrom":[subQ1,subQ0]});Q2=makeQuery(id+"F5.imprint","IMPRINT",FACE,{"disambiguationData":[TD([[makeQuery(id+"F5.imprint","IMPRINT",EDGE,{"disambiguationData":[TD([[subQ2,1.0]])],"derivedFrom":subQ1}),1.0]])]});}
            var Q3;
            {var subQ0=sQuery(id+"F5.wireOp",EDGE,"E36");var subQ1=sQuery(id+"F5.wireOp",EDGE,"E32");var subQ2=makeQuery(id+"F5.imprint","INTERSECT",VERTEX,{"disambiguationData":[OD(1.0)],"derivedFrom":[subQ1,subQ0]});Q3=makeQuery(id+"F5.imprint","IMPRINT",FACE,{"disambiguationData":[TD([[makeQuery(id+"F5.imprint","IMPRINT",EDGE,{"disambiguationData":[TD([[subQ2,-1.0]])],"derivedFrom":subQ1}),1.0]])]});}
            extrude(context, id + "F6", {"entities" : qUnion([Q0, Q1, Q2, Q3]), "operationType" : NewBodyOperationType.REMOVE, "endBound" : BoundingType.UP_TO_NEXT, "oppositeDirection" : true, "depth" : 25 * mm, "offsetDistance" : 25 * mm});
        }
        {
            var Q0;
            Q0=makeQuery(id+"F1.opExtrude","CAP_FACE",FACE,{"disambiguationData":[OSD([sQuery(id+"F0.wireOp",EDGE,"E1.bottom"),sQuery(id+"F0.wireOp",EDGE,"E1.top"),sQuery(id+"F0.wireOp",EDGE,"E1.left"),sQuery(id+"F0.wireOp",EDGE,"E1.right")])],"isStart":false});
            var sketch = newSketch(context, id + "F7", { "sketchPlane" : qUnion([Q0])});
            skCircle(sketch, "E41", {"center": v(-42, 0) * mm, "radius": 2.6 * mm});
            skCircle(sketch, "E42", {"center": v(0, 42) * mm, "radius": 2.6 * mm});
            skCircle(sketch, "E43", {"center": v(42, 0) * mm, "radius": 2.6 * mm});
            skCircle(sketch, "E44", {"center": v(0, -42) * mm, "radius": 2.6 * mm});
            skSolve(sketch);
        }
        {
            var Q0;
            Q0 = qSketchRegion(id + "F7", true);
            extrude(context, id + "F8", {"entities" : qUnion([Q0]), "operationType" : NewBodyOperationType.REMOVE, "endBound" : BoundingType.UP_TO_NEXT, "oppositeDirection" : true, "depth" : 25 * mm, "offsetDistance" : 25 * mm});
        }
    });
